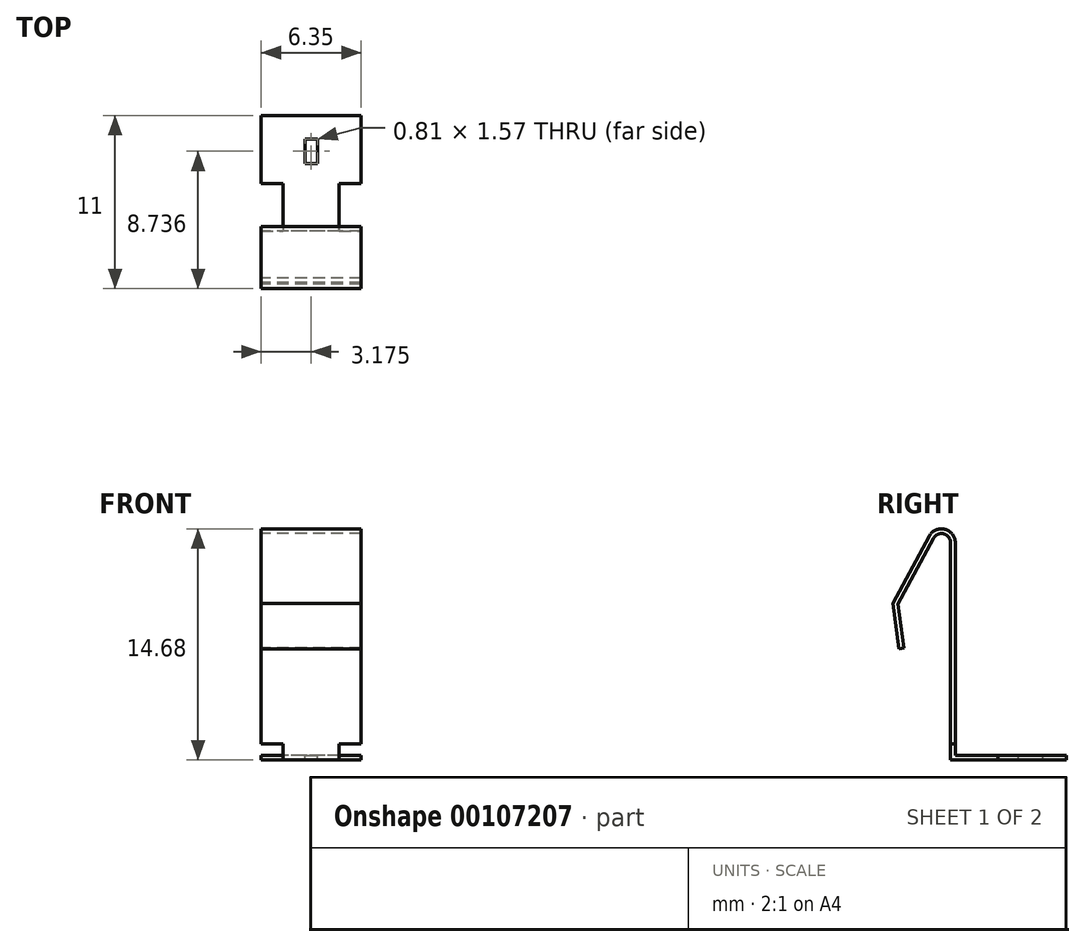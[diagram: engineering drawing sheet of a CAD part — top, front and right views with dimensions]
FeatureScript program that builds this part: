
annotation { "Feature Type Name" : "Feature", "Feature Type Description" : "" }
export const myFeature = defineFeature(function(context is Context, id is Id, definition is map)
    precondition{}
    {
        {
            var Q0;
            Q0=qCreatedBy(makeId("Right.planeOp"),FACE);
            var sketch = newSketch(context, id + "F0", { "sketchPlane" : qUnion([Q0])});
            skLineSegment(sketch, "E0", {"start": v(0, 0) * mm, "end": v(-7.34, 0) * mm});
            skLineSegment(sketch, "E1", {"start": v(-7.34, 0) * mm, "end": v(-7.34, 13.8) * mm});
            skArc(sketch, "E2", {"start": v(-7.34, 13.8) * mm, "mid": v(-7.78, 14.36) * mm, "end": v(-8.43, 14.08) * mm});
            skLineSegment(sketch, "E3", {"start": v(-8.43, 14.08) * mm, "end": v(-10.69, 9.9) * mm});
            skLineSegment(sketch, "E4", {"start": v(-10.69, 9.9) * mm, "end": v(-10.3, 7.1) * mm});
            skLineSegment(sketch, "E5", {"start": v(-10.3, 7.1) * mm, "end": v(-10.6, 7.06) * mm});
            skLineSegment(sketch, "E6", {"start": v(-10.6, 7.06) * mm, "end": v(-11, 9.96) * mm});
            skLineSegment(sketch, "E7", {"start": v(-11, 9.96) * mm, "end": v(-8.7, 14.22) * mm});
            skLineSegment(sketch, "E8", {"start": v(0, 0) * mm, "end": v(0, 0.3) * mm});
            skLineSegment(sketch, "E9", {"start": v(0, 0.3) * mm, "end": v(-7.04, 0.3) * mm});
            skLineSegment(sketch, "E10", {"start": v(-7.04, 0.3) * mm, "end": v(-7.04, 13.8) * mm});
            skArc(sketch, "E11", {"start": v(-7.04, 13.8) * mm, "mid": v(-7.7, 14.65) * mm, "end": v(-8.7, 14.22) * mm});
            skSolve(sketch);
        }
        {
            var Q0;
            Q0=makeQuery(id+"F0.imprint","IMPRINT",FACE,{"disambiguationData":[TD([[makeQuery(id+"F0.imprint","IMPRINT",EDGE,{"derivedFrom":sQuery(id+"F0.wireOp",EDGE,"E0")}),-1.0]])]});
            extrude(context, id + "F1", {"entities" : qUnion([Q0]), "depth" : 6.35 * mm});
        }
        {
            var Q0;
            Q0=makeQuery(id+"F1.opExtrude","SWEPT_FACE",FACE,{"disambiguationData":[OSD([sQuery(id+"F0.wireOp",EDGE,"E1")])]});
            var sketch = newSketch(context, id + "F2", { "sketchPlane" : qUnion([Q0])});
            skLineSegment(sketch, "E12.bottom", {"start": v(4.95, 0.3) * mm, "end": v(6.35, 0.3) * mm});
            skLineSegment(sketch, "E12.top", {"start": v(4.96, 1) * mm, "end": v(6.35, 1) * mm});
            skLineSegment(sketch, "E12.left", {"start": v(4.96, 0.3) * mm, "end": v(4.96, 1) * mm});
            skLineSegment(sketch, "E12.right", {"start": v(6.35, 0.3) * mm, "end": v(6.35, 1) * mm});
            skLineSegment(sketch, "E13.bottom", {"start": v(0, 0.3) * mm, "end": v(1.4, 0.3) * mm});
            skLineSegment(sketch, "E13.top", {"start": v(0, 1) * mm, "end": v(1.4, 1) * mm});
            skLineSegment(sketch, "E13.left", {"start": v(0, 0.3) * mm, "end": v(0, 1) * mm});
            skLineSegment(sketch, "E13.right", {"start": v(1.4, 0.3) * mm, "end": v(1.4, 1) * mm});
            skLineSegment(sketch, "E14", {"start": v(0, 1) * mm, "end": v(6.35, 1) * mm, "construction": true});
            skLineSegment(sketch, "E15", {"start": v(3.17, 1) * mm, "end": v(3.17, 0) * mm, "construction": true});
            skLineSegment(sketch, "E16", {"start": v(1.4, 0.3) * mm, "end": v(4.95, 0.3) * mm, "construction": true});
            skPoint(sketch, "E17", {"position": v(3.17, 0.3) * mm});
            skSolve(sketch);
        }
        {
            var Q0;
            Q0 = qSketchRegion(id + "F2", true);
            extrude(context, id + "F3", {"entities" : qUnion([Q0]), "operationType" : NewBodyOperationType.REMOVE, "endBound" : BoundingType.UP_TO_NEXT, "oppositeDirection" : true, "depth" : 25 * mm});
        }
        {
            var Q0;
            Q0=makeQuery(id+"F3.boolean.opBoolean","MERGE",FACE,{"derivedFrom":[makeQuery(id+"F1.opExtrude","SWEPT_FACE",FACE,{"disambiguationData":[OSD([sQuery(id+"F0.wireOp",EDGE,"E9")])]}),makeQuery(id+"F3.opExtrude","SWEPT_FACE",FACE,{"disambiguationData":[OSD([sQuery(id+"F2.wireOp",EDGE,"E12.bottom")])]}),makeQuery(id+"F3.opExtrude","SWEPT_FACE",FACE,{"disambiguationData":[OSD([sQuery(id+"F2.wireOp",EDGE,"E13.bottom")])]})]});
            var sketch = newSketch(context, id + "F4", { "sketchPlane" : qUnion([Q0])});
            skPoint(sketch, "E18.oppositeSnap0", {"position": v(1.4, -7.19) * mm});
            skLineSegment(sketch, "E18.bottom", {"start": v(0, -7.34) * mm, "end": v(1.4, -7.34) * mm});
            skLineSegment(sketch, "E18.top", {"start": v(0, -4.32) * mm, "end": v(1.4, -4.32) * mm});
            skLineSegment(sketch, "E18.left", {"start": v(0, -7.34) * mm, "end": v(0, -4.32) * mm});
            skLineSegment(sketch, "E18.right", {"start": v(1.4, -7.34) * mm, "end": v(1.4, -4.32) * mm});
            skLineSegment(sketch, "E19.bottom", {"start": v(6.35, -7.34) * mm, "end": v(4.96, -7.34) * mm});
            skLineSegment(sketch, "E19.top", {"start": v(6.35, -4.32) * mm, "end": v(4.96, -4.32) * mm});
            skLineSegment(sketch, "E19.left", {"start": v(6.35, -7.34) * mm, "end": v(6.35, -4.32) * mm});
            skLineSegment(sketch, "E19.right", {"start": v(4.96, -7.34) * mm, "end": v(4.96, -4.32) * mm});
            skLineSegment(sketch, "E20", {"start": v(3.17, 0) * mm, "end": v(3.17, -2.26) * mm, "construction": true});
            skLineSegment(sketch, "E21.bottom", {"start": v(2.77, -1.48) * mm, "end": v(3.58, -1.48) * mm});
            skLineSegment(sketch, "E21.top", {"start": v(2.77, -3.05) * mm, "end": v(3.58, -3.05) * mm});
            skLineSegment(sketch, "E21.left", {"start": v(2.77, -1.48) * mm, "end": v(2.77, -3.05) * mm});
            skLineSegment(sketch, "E21.right", {"start": v(3.58, -1.48) * mm, "end": v(3.58, -3.05) * mm});
            skPoint(sketch, "E21.middle", {"position": v(3.17, -2.26) * mm});
            skSolve(sketch);
        }
        {
            var Q0;
            {var subQ3=sQuery(id+"F4.wireOp",EDGE,"E18.bottom");Q0=makeQuery(id+"F4.imprint","IMPRINT",FACE,{"disambiguationData":[TD([[makeQuery(id+"F4.imprint","IMPRINT",EDGE,{"derivedFrom":subQ3}),1.0]])]});}
            var Q1;
            {var subQ3=sQuery(id+"F4.wireOp",EDGE,"E19.bottom");Q1=makeQuery(id+"F4.imprint","IMPRINT",FACE,{"disambiguationData":[TD([[makeQuery(id+"F4.imprint","IMPRINT",EDGE,{"derivedFrom":subQ3}),1.0]])]});}
            var Q2;
            Q2=makeQuery(id+"F4.imprint","IMPRINT",FACE,{"disambiguationData":[TD([[makeQuery(id+"F4.imprint","IMPRINT",EDGE,{"derivedFrom":sQuery(id+"F4.wireOp",EDGE,"E21.bottom")}),-1.0]])]});
            extrude(context, id + "F5", {"entities" : qUnion([Q0, Q1, Q2]), "operationType" : NewBodyOperationType.REMOVE, "endBound" : BoundingType.UP_TO_NEXT, "oppositeDirection" : true, "depth" : 25 * mm});
        }
    });
